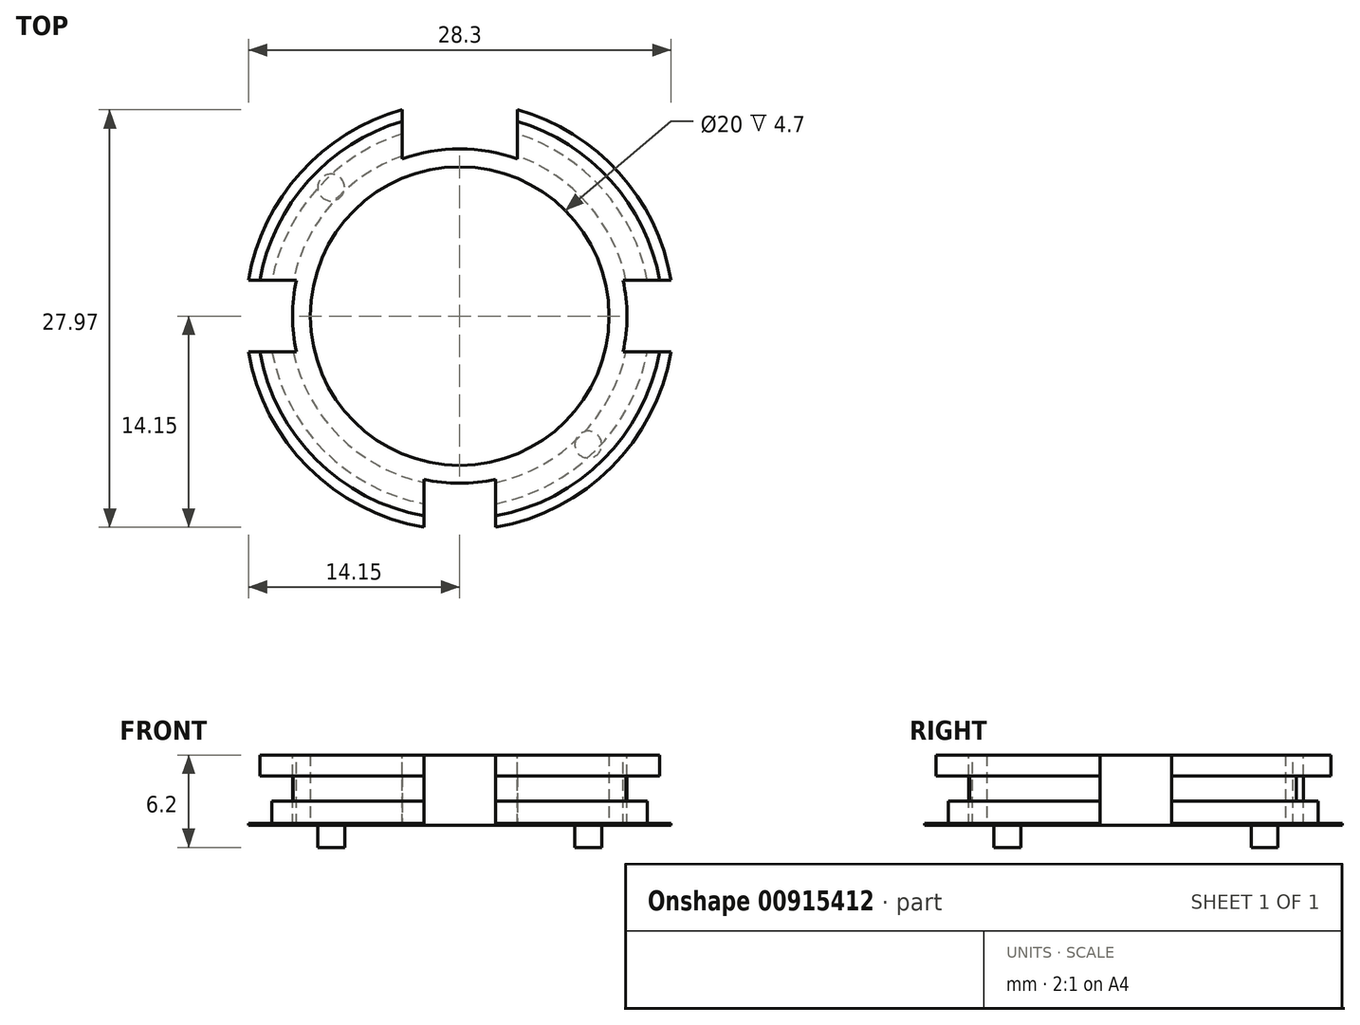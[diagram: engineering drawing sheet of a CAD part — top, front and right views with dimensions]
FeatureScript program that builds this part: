
annotation { "Feature Type Name" : "Feature", "Feature Type Description" : "" }
export const myFeature = defineFeature(function(context is Context, id is Id, definition is map)
    precondition{}
    {
        {
            var Q0;
            Q0=qCreatedBy(makeId("Top.planeOp"),FACE);
            var sketch = newSketch(context, id + "F0", { "sketchPlane" : qUnion([Q0])});
            skCircle(sketch, "E0", {"center": v(0, 0) * mm, "radius": 10 * mm});
            skCircle(sketch, "E1.0", {"center": v(0, 0) * mm, "radius": 11.4 * mm});
            skSolve(sketch);
        }
        {
            var Q0;
            Q0=makeQuery(id+"F0.imprint","IMPRINT",FACE,{"disambiguationData":[TD([[makeQuery(id+"F0.imprint","IMPRINT",EDGE,{"derivedFrom":sQuery(id+"F0.wireOp",EDGE,"E0")}),-1.0]])]});
            extrude(context, id + "F1", {"entities" : qUnion([Q0]), "depth" : 6.2 * mm, "offsetDistance" : 25 * mm});
        }
        {
            var Q0;
            Q0=makeQuery(id+"F1.opExtrude","CAP_FACE",FACE,{"disambiguationData":[OSD([sQuery(id+"F0.wireOp",EDGE,"E0"),sQuery(id+"F0.wireOp",EDGE,"E1.0")])],"isStart":false});
            var sketch = newSketch(context, id + "F2", { "sketchPlane" : qUnion([Q0])});
            skCircle(sketch, "E2.0", {"center": v(0, 0) * mm, "radius": 13.6 * mm});
            skSolve(sketch);
        }
        {
            var Q0;
            Q0=makeQuery(id+"F2.imprint","IMPRINT",FACE,{"disambiguationData":[TD([[makeQuery(id+"F2.imprint","IMPRINT",EDGE,{"derivedFrom":sQuery(id+"F2.wireOp",EDGE,"E2.0")}),1.0]])]});
            extrude(context, id + "F3", {"entities" : qUnion([Q0]), "operationType" : NewBodyOperationType.ADD, "oppositeDirection" : true, "depth" : 1.4 * mm, "offsetDistance" : 25 * mm});
        }
        {
            var Q0;
            Q0=makeQuery(id+"F1.opExtrude","CAP_FACE",FACE,{"disambiguationData":[OSD([sQuery(id+"F0.wireOp",EDGE,"E0"),sQuery(id+"F0.wireOp",EDGE,"E1.0")])],"isStart":true});
            var sketch = newSketch(context, id + "F4", { "sketchPlane" : qUnion([Q0])});
            skCircle(sketch, "E3", {"center": v(0, 0) * mm, "radius": 14.35 * mm});
            skSolve(sketch);
        }
        {
            var Q0;
            Q0=makeQuery(id+"F4.imprint","IMPRINT",FACE,{"disambiguationData":[TD([[makeQuery(id+"F4.imprint","IMPRINT",EDGE,{"derivedFrom":sQuery(id+"F4.wireOp",EDGE,"E3")}),1.0]])]});
            extrude(context, id + "F5", {"entities" : qUnion([Q0]), "operationType" : NewBodyOperationType.ADD, "oppositeDirection" : true, "depth" : 1.6 * mm, "offsetDistance" : 25 * mm});
        }
        {
            var Q0;
            Q0=makeQuery(id+"F5.opExtrude","CAP_FACE",FACE,{"disambiguationData":[OSD([sQuery(id+"F0.wireOp",EDGE,"E1.0"),sQuery(id+"F4.wireOp",EDGE,"E3")])],"isStart":false});
            var sketch = newSketch(context, id + "F6", { "sketchPlane" : qUnion([Q0])});
            skCircle(sketch, "E4", {"center": v(0, 0) * mm, "radius": 12.8 * mm});
            skSolve(sketch);
        }
        {
            var Q0;
            Q0=makeQuery(id+"F6.imprint","IMPRINT",FACE,{"disambiguationData":[TD([[makeQuery(id+"F6.imprint","IMPRINT",EDGE,{"derivedFrom":sQuery(id+"F6.wireOp",EDGE,"E4")}),1.0]])]});
            extrude(context, id + "F7", {"entities" : qUnion([Q0]), "operationType" : NewBodyOperationType.ADD, "depth" : 1.5 * mm, "offsetDistance" : 25 * mm});
        }
        {
            var Q0;
            {var subQ0=sQuery(id+"F0.wireOp",EDGE,"E1.0");Q0=makeQuery(id+"F3.boolean.opBoolean","MERGE",FACE,{"derivedFrom":[makeQuery(id+"F1.opExtrude","CAP_FACE",FACE,{"disambiguationData":[OSD([sQuery(id+"F0.wireOp",EDGE,"E0"),subQ0])],"isStart":false}),makeQuery(id+"F3.opExtrude","CAP_FACE",FACE,{"disambiguationData":[OSD([subQ0,sQuery(id+"F2.wireOp",EDGE,"E2.0")])],"isStart":true})]});}
            var sketch = newSketch(context, id + "F8", { "sketchPlane" : qUnion([Q0])});
            skCircle(sketch, "E5.0", {"center": v(0, 0) * mm, "radius": 11.2 * mm});
            skLineSegment(sketch, "E6", {"start": v(0, -11.2) * mm, "end": v(0, 17.2) * mm, "construction": true});
            skLineSegment(sketch, "E7", {"start": v(0, -11.2) * mm, "end": v(0, -18.74) * mm, "construction": true});
            skLineSegment(sketch, "E8", {"start": v(-19.22, 0) * mm, "end": v(24.18, 0) * mm, "construction": true});
            skLineSegment(sketch, "E9", {"start": v(-3.85, 11.2) * mm, "end": v(-3.85, 16.07) * mm});
            skLineSegment(sketch, "E10.MirrorCS", {"start": v(3.85, 11.2) * mm, "end": v(3.85, 16.07) * mm});
            skLineSegment(sketch, "E11", {"start": v(-3.85, 16.07) * mm, "end": v(3.85, 16.07) * mm});
            skLineSegment(sketch, "E12", {"start": v(-3.85, 11.2) * mm, "end": v(-3.85, 10.52) * mm});
            skLineSegment(sketch, "E13", {"start": v(3.85, 11.2) * mm, "end": v(3.85, 10.52) * mm});
            skPoint(sketch, "E14.start.orphan", {"position": v(0, 11.2) * mm});
            skLineSegment(sketch, "E15", {"start": v(2.4, -11.2) * mm, "end": v(2.4, -15.22) * mm});
            skLineSegment(sketch, "E16.MirrorCS", {"start": v(-2.4, -11.2) * mm, "end": v(-2.4, -15.22) * mm});
            skLineSegment(sketch, "E17", {"start": v(-2.4, -15.22) * mm, "end": v(2.4, -15.22) * mm});
            skLineSegment(sketch, "E18", {"start": v(-2.4, -11.2) * mm, "end": v(-2.4, -10.94) * mm});
            skLineSegment(sketch, "E19", {"start": v(2.4, -11.2) * mm, "end": v(2.4, -10.94) * mm});
            skPoint(sketch, "E20.MirrorCS.start.orphan", {"position": v(0, -11.2) * mm});
            skLineSegment(sketch, "E21", {"start": v(-11.2, 2.4) * mm, "end": v(-16.22, 2.4) * mm});
            skLineSegment(sketch, "E22.MirrorCS", {"start": v(-11.2, -2.4) * mm, "end": v(-16.22, -2.4) * mm});
            skLineSegment(sketch, "E23", {"start": v(-11.2, -2.4) * mm, "end": v(-10.94, -2.4) * mm});
            skLineSegment(sketch, "E24", {"start": v(-11.2, 2.4) * mm, "end": v(-10.94, 2.4) * mm});
            skPoint(sketch, "E25.start.orphan", {"position": v(-11.2, 0) * mm});
            skPoint(sketch, "E26.MirrorCS.end.orphan", {"position": v(-11.2, -2.4) * mm});
            skLineSegment(sketch, "E27", {"start": v(-16.22, -2.4) * mm, "end": v(-16.22, 2.4) * mm});
            skLineSegment(sketch, "E28.MirrorCS", {"start": v(11.2, 2.4) * mm, "end": v(10.94, 2.4) * mm});
            skLineSegment(sketch, "E29.MirrorCS", {"start": v(11.2, 2.4) * mm, "end": v(16.22, 2.4) * mm});
            skLineSegment(sketch, "E30.MirrorCS", {"start": v(11.2, -2.4) * mm, "end": v(16.22, -2.4) * mm});
            skLineSegment(sketch, "E31.MirrorCS", {"start": v(11.2, -2.4) * mm, "end": v(10.94, -2.4) * mm});
            skLineSegment(sketch, "E32.MirrorCS", {"start": v(16.22, -2.4) * mm, "end": v(16.22, 2.4) * mm});
            skSolve(sketch);
        }
        {
            var Q0;
            {var subQ4=sQuery(id+"F8.wireOp",EDGE,"E12");Q0=makeQuery(id+"F8.imprint","IMPRINT",FACE,{"disambiguationData":[TD([[makeQuery(id+"F8.imprint","IMPRINT",EDGE,{"derivedFrom":subQ4}),1.0]])]});}
            var Q1;
            {var subQ0=sQuery(id+"F8.wireOp",EDGE,"E11");Q1=makeQuery(id+"F8.imprint","IMPRINT",FACE,{"disambiguationData":[TD([[makeQuery(id+"F8.imprint","IMPRINT",EDGE,{"derivedFrom":subQ0}),-1.0]])]});}
            var Q2;
            {var subQ0=sQuery(id+"F8.wireOp",EDGE,"E27");Q2=makeQuery(id+"F8.imprint","IMPRINT",FACE,{"disambiguationData":[TD([[makeQuery(id+"F8.imprint","IMPRINT",EDGE,{"derivedFrom":subQ0}),-1.0]])]});}
            var Q3;
            {var subQ0=sQuery(id+"F8.wireOp",EDGE,"E23");Q3=makeQuery(id+"F8.imprint","IMPRINT",FACE,{"disambiguationData":[TD([[makeQuery(id+"F8.imprint","IMPRINT",EDGE,{"derivedFrom":subQ0}),1.0]])]});}
            var Q4;
            {var subQ1=sQuery(id+"F8.wireOp",EDGE,"E28.MirrorCS");Q4=makeQuery(id+"F8.imprint","IMPRINT",FACE,{"disambiguationData":[TD([[makeQuery(id+"F8.imprint","IMPRINT",EDGE,{"derivedFrom":subQ1}),1.0]])]});}
            var Q5;
            {var subQ0=sQuery(id+"F8.wireOp",EDGE,"E32.MirrorCS");Q5=makeQuery(id+"F8.imprint","IMPRINT",FACE,{"disambiguationData":[TD([[makeQuery(id+"F8.imprint","IMPRINT",EDGE,{"derivedFrom":subQ0}),1.0]])]});}
            var Q6;
            {var subQ0=sQuery(id+"F8.wireOp",EDGE,"E18");Q6=makeQuery(id+"F8.imprint","IMPRINT",FACE,{"disambiguationData":[TD([[makeQuery(id+"F8.imprint","IMPRINT",EDGE,{"derivedFrom":subQ0}),-1.0]])]});}
            var Q7;
            {var subQ0=sQuery(id+"F8.wireOp",EDGE,"E17");Q7=makeQuery(id+"F8.imprint","IMPRINT",FACE,{"disambiguationData":[TD([[makeQuery(id+"F8.imprint","IMPRINT",EDGE,{"derivedFrom":subQ0}),1.0]])]});}
            extrude(context, id + "F9", {"entities" : qUnion([Q0, Q1, Q2, Q3, Q4, Q5, Q6, Q7]), "operationType" : NewBodyOperationType.REMOVE, "oppositeDirection" : true, "depth" : 25 * mm, "offsetDistance" : 25 * mm});
        }
        {
            var Q0;
            {var subQ0=sQuery(id+"F0.wireOp",EDGE,"E1.0");Q0=makeQuery(id+"F5.boolean.opBoolean","MERGE",FACE,{"derivedFrom":[makeQuery(id+"F1.opExtrude","CAP_FACE",FACE,{"disambiguationData":[OSD([sQuery(id+"F0.wireOp",EDGE,"E0"),subQ0])],"isStart":true}),makeQuery(id+"F5.opExtrude","CAP_FACE",FACE,{"disambiguationData":[OSD([subQ0,sQuery(id+"F4.wireOp",EDGE,"E3")])],"isStart":true})]});}
            var sketch = newSketch(context, id + "F10", { "sketchPlane" : qUnion([Q0])});
            skLineSegment(sketch, "E33", {"start": v(0, 0) * mm, "end": v(-13.78, 13.78) * mm, "construction": true});
            skLineSegment(sketch, "E34", {"start": v(0, 18.75) * mm, "end": v(0, -19.27) * mm, "construction": true});
            skLineSegment(sketch, "E35", {"start": v(-19.96, 0) * mm, "end": v(23.65, 0) * mm, "construction": true});
            skLineSegment(sketch, "E36", {"start": v(-10.15, 10.15) * mm, "end": v(-7.07, 7.07) * mm});
            skCircle(sketch, "E37", {"center": v(-8.6, 8.6) * mm, "radius": 0.9 * mm});
            skCircle(sketch, "E38.MirrorC", {"center": v(8.6, 8.6) * mm, "radius": 0.9 * mm});
            skCircle(sketch, "E39.MirrorC", {"center": v(8.6, -8.6) * mm, "radius": 0.9 * mm});
            skCircle(sketch, "E40.MirrorC", {"center": v(-8.6, -8.6) * mm, "radius": 0.9 * mm});
            skSolve(sketch);
        }
        {
            var Q0;
            {var subQ0=sQuery(id+"F10.wireOp",EDGE,"E37");var subQ1=sQuery(id+"F10.wireOp",EDGE,"E36");var subQ2=makeQuery(id+"F10.imprint","INTERSECT",VERTEX,{"disambiguationData":[OD(0.0)],"derivedFrom":[subQ1,subQ0]});Q0=makeQuery(id+"F10.imprint","IMPRINT",FACE,{"disambiguationData":[TD([[makeQuery(id+"F10.imprint","IMPRINT",EDGE,{"disambiguationData":[TD([[subQ2,-1.0]])],"derivedFrom":subQ1}),1.0]])]});}
            var Q1;
            {var subQ0=sQuery(id+"F10.wireOp",EDGE,"E37");var subQ1=sQuery(id+"F10.wireOp",EDGE,"E36");var subQ2=makeQuery(id+"F10.imprint","INTERSECT",VERTEX,{"disambiguationData":[OD(0.0)],"derivedFrom":[subQ1,subQ0]});Q1=makeQuery(id+"F10.imprint","IMPRINT",FACE,{"disambiguationData":[TD([[makeQuery(id+"F10.imprint","IMPRINT",EDGE,{"disambiguationData":[TD([[subQ2,-1.0]])],"derivedFrom":subQ1}),-1.0]])]});}
            var Q2;
            Q2=makeQuery(id+"F10.imprint","IMPRINT",FACE,{"disambiguationData":[TD([[makeQuery(id+"F10.imprint","IMPRINT",EDGE,{"derivedFrom":sQuery(id+"F10.wireOp",EDGE,"E38.MirrorC")}),-1.0]])]});
            var Q3;
            Q3=makeQuery(id+"F10.imprint","IMPRINT",FACE,{"disambiguationData":[TD([[makeQuery(id+"F10.imprint","IMPRINT",EDGE,{"derivedFrom":sQuery(id+"F10.wireOp",EDGE,"E39.MirrorC")}),1.0]])]});
            var Q4;
            Q4=makeQuery(id+"F10.imprint","IMPRINT",FACE,{"disambiguationData":[TD([[makeQuery(id+"F10.imprint","IMPRINT",EDGE,{"derivedFrom":sQuery(id+"F10.wireOp",EDGE,"E40.MirrorC")}),-1.0]])]});
            extrude(context, id + "F11", {"entities" : qUnion([Q0, Q1, Q2, Q3, Q4]), "operationType" : NewBodyOperationType.REMOVE, "oppositeDirection" : true, "depth" : 1.5 * mm, "offsetDistance" : 25 * mm});
        }
    });
